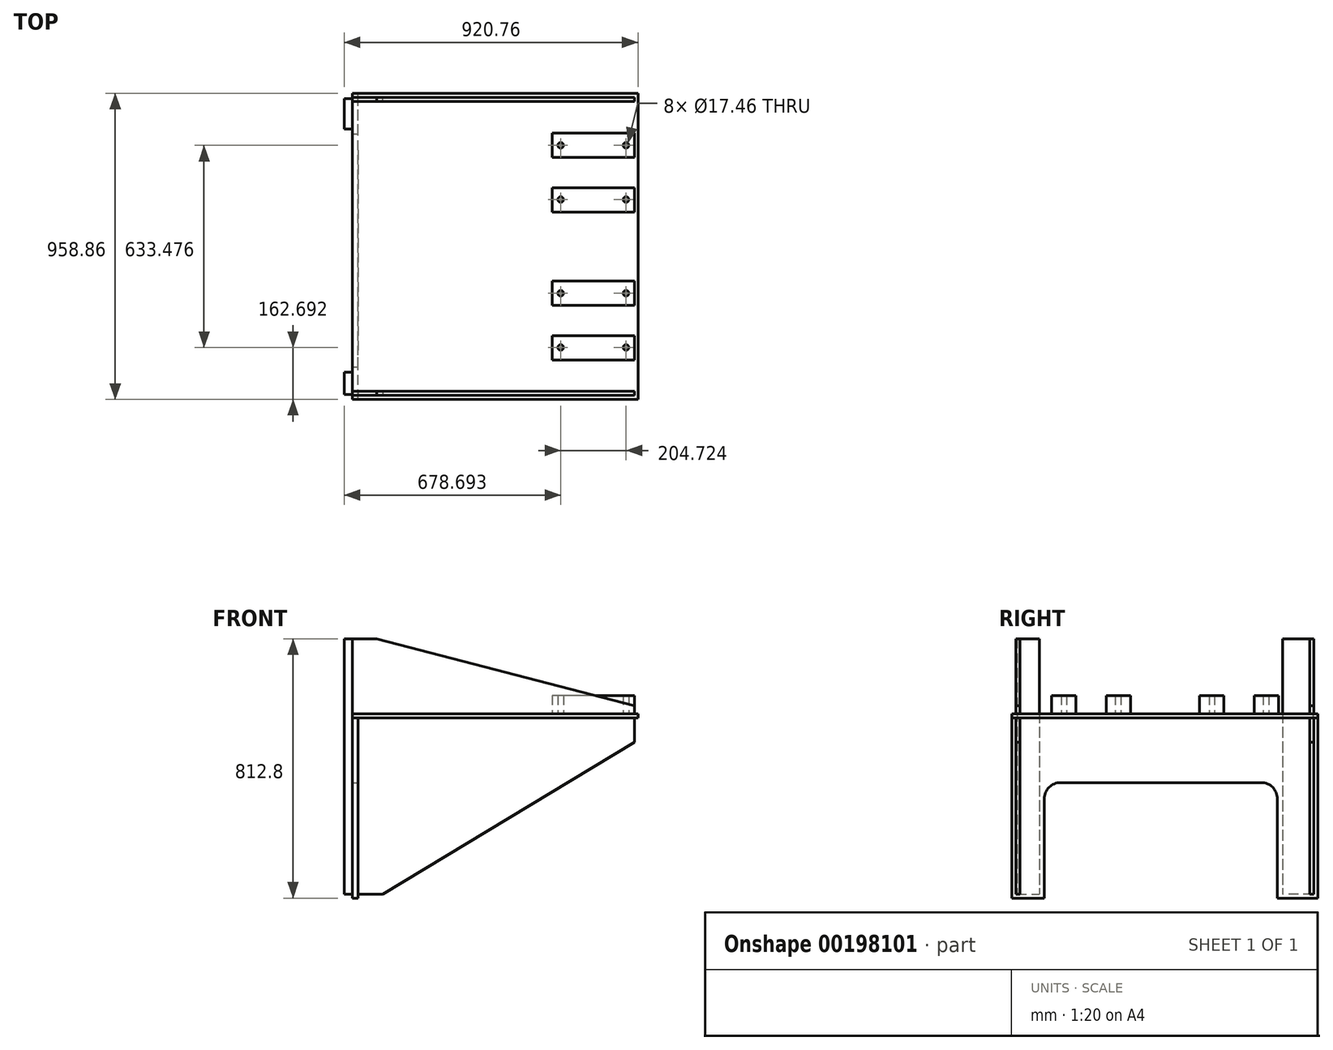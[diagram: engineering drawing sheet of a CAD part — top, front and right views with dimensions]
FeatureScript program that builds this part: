
annotation { "Feature Type Name" : "Feature", "Feature Type Description" : "" }
export const myFeature = defineFeature(function(context is Context, id is Id, definition is map)
    precondition{}
    {
        {
            var Q0;
            Q0=qCreatedBy(makeId("Top.planeOp"),FACE);
            var sketch = newSketch(context, id + "F0", { "sketchPlane" : qUnion([Q0])});
            skLineSegment(sketch, "E0.bottom", {"start": v(-447.67, 479.43) * mm, "end": v(447.68, 479.43) * mm});
            skLineSegment(sketch, "E0.top", {"start": v(-447.68, -479.43) * mm, "end": v(447.68, -479.43) * mm});
            skLineSegment(sketch, "E0.left", {"start": v(-447.67, 479.43) * mm, "end": v(-447.68, -479.43) * mm});
            skLineSegment(sketch, "E0.right", {"start": v(447.68, 479.42) * mm, "end": v(447.68, -479.43) * mm});
            skPoint(sketch, "E0.middle", {"position": v(0, 0) * mm});
            skSolve(sketch);
        }
        {
            var Q0;
            Q0 = qSketchRegion(id + "F0", true);
            extrude(context, id + "F1", {"entities" : qUnion([Q0]), "depth" : 12.7 * mm});
        }
        {
            var Q0;
            Q0=makeQuery(id+"F1.opExtrude","CAP_FACE",FACE,{"disambiguationData":[OSD([sQuery(id+"F0.wireOp",EDGE,"E0.bottom"),sQuery(id+"F0.wireOp",EDGE,"E0.top"),sQuery(id+"F0.wireOp",EDGE,"E0.left"),sQuery(id+"F0.wireOp",EDGE,"E0.right")])],"isStart":false});
            var sketch = newSketch(context, id + "F2", { "sketchPlane" : qUnion([Q0])});
            skLineSegment(sketch, "E1", {"start": v(-705.76, 0) * mm, "end": v(723.96, 0) * mm, "construction": true});
            skLineSegment(sketch, "E2.0", {"start": v(-447.68, -479.43) * mm, "end": v(447.68, -479.43) * mm, "construction": true});
            skLineSegment(sketch, "E3.0", {"start": v(-447.68, -466.73) * mm, "end": v(447.68, -466.73) * mm, "construction": true});
            skLineSegment(sketch, "E4.0", {"start": v(447.68, 479.42) * mm, "end": v(447.68, -479.43) * mm, "construction": true});
            skLineSegment(sketch, "E5.0", {"start": v(436.5, 479.42) * mm, "end": v(436.5, -479.43) * mm, "construction": true});
            skLineSegment(sketch, "E6.0", {"start": v(-447.67, 479.43) * mm, "end": v(-447.68, -479.43) * mm, "construction": true});
            skLineSegment(sketch, "E7.bottom", {"start": v(436.5, -466.73) * mm, "end": v(-447.68, -466.73) * mm});
            skLineSegment(sketch, "E7.top", {"start": v(436.5, -454.03) * mm, "end": v(-447.68, -454.03) * mm});
            skLineSegment(sketch, "E7.left", {"start": v(436.5, -466.73) * mm, "end": v(436.5, -454.03) * mm});
            skLineSegment(sketch, "E7.right", {"start": v(-447.68, -466.73) * mm, "end": v(-447.68, -454.03) * mm});
            skSolve(sketch);
        }
        {
            var Q0;
            Q0 = qSketchRegion(id + "F2", true);
            extrude(context, id + "F3", {"entities" : qUnion([Q0]), "depth" : 234.95 * mm});
        }
        {
            var Q0;
            Q0=makeQuery(id+"F3.opExtrude","SWEPT_FACE",FACE,{"disambiguationData":[OSD([sQuery(id+"F2.wireOp",EDGE,"E7.bottom")])]});
            var sketch = newSketch(context, id + "F4", { "sketchPlane" : qUnion([Q0])});
            skLineSegment(sketch, "E8.0", {"start": v(-447.68, 247.65) * mm, "end": v(-447.68, 12.7) * mm, "construction": true});
            skLineSegment(sketch, "E9.0", {"start": v(-447.68, 12.7) * mm, "end": v(447.68, 12.7) * mm, "construction": true});
            skLineSegment(sketch, "E10.0", {"start": v(-371.48, 247.65) * mm, "end": v(-371.48, 12.7) * mm, "construction": true});
            skLineSegment(sketch, "E11.0", {"start": v(-447.68, 38.1) * mm, "end": v(447.68, 38.1) * mm, "construction": true});
            skLineSegment(sketch, "E12", {"start": v(-371.48, 247.65) * mm, "end": v(436.5, 38.1) * mm});
            skLineSegment(sketch, "E13", {"start": v(436.5, 38.1) * mm, "end": v(436.5, 247.65) * mm});
            skLineSegment(sketch, "E14", {"start": v(436.5, 247.65) * mm, "end": v(-371.48, 247.65) * mm});
            skSolve(sketch);
        }
        {
            var Q0;
            Q0 = qSketchRegion(id + "F4", true);
            extrude(context, id + "F5", {"entities" : qUnion([Q0]), "operationType" : NewBodyOperationType.REMOVE, "endBound" : BoundingType.THROUGH_ALL, "oppositeDirection" : true, "depth" : 25.4 * mm});
        }
        {
            var Q0;
            Q0=makeQuery(id+"F3.opExtrude","SWEPT_BODY",BODY,{"disambiguationData":[OSD([sQuery(id+"F2.wireOp",EDGE,"E7.bottom"),sQuery(id+"F2.wireOp",EDGE,"E7.top"),sQuery(id+"F2.wireOp",EDGE,"E7.left"),sQuery(id+"F2.wireOp",EDGE,"E7.right")])]});
            var Q1;
            Q1=qCreatedBy(makeId("Front.planeOp"),FACE);
            mirror(context, id + "F6", {"entities" : qUnion([Q0]), "mirrorPlane" : qUnion([Q1])});
        }
        {
            var Q0;
            Q0=makeQuery(id+"F3.opExtrude","SWEPT_FACE",FACE,{"disambiguationData":[OSD([sQuery(id+"F2.wireOp",EDGE,"E7.bottom")])]});
            var sketch = newSketch(context, id + "F7", { "sketchPlane" : qUnion([Q0])});
            skLineSegment(sketch, "E15.0", {"start": v(436.5, 38.1) * mm, "end": v(436.5, -76.2) * mm, "construction": true});
            skLineSegment(sketch, "E16", {"start": v(-447.68, 22.62) * mm, "end": v(-447.68, -552.45) * mm, "construction": true});
            skLineSegment(sketch, "E17.0", {"start": v(-447.68, 0) * mm, "end": v(447.68, 0) * mm, "construction": true});
            skLineSegment(sketch, "E18.0", {"start": v(-447.68, -552.45) * mm, "end": v(447.68, -552.45) * mm, "construction": true});
            skPoint(sketch, "E19.orphan", {"position": v(436.5, 12.7) * mm});
            skLineSegment(sketch, "E20.0", {"start": v(-428.63, 22.62) * mm, "end": v(-428.63, -552.45) * mm, "construction": true});
            skLineSegment(sketch, "E21.bottom", {"start": v(-428.63, -552.45) * mm, "end": v(436.5, -552.45) * mm});
            skLineSegment(sketch, "E21.top", {"start": v(-428.63, 0) * mm, "end": v(436.5, 0) * mm});
            skLineSegment(sketch, "E21.left", {"start": v(-428.63, -552.45) * mm, "end": v(-428.63, 0) * mm});
            skLineSegment(sketch, "E21.right", {"start": v(436.5, -76.2) * mm, "end": v(436.5, 0) * mm});
            skLineSegment(sketch, "E22.0", {"start": v(-447.68, -76.2) * mm, "end": v(447.68, -76.2) * mm, "construction": true});
            skLineSegment(sketch, "E23.0", {"start": v(-352.43, 22.62) * mm, "end": v(-352.43, -552.45) * mm, "construction": true});
            skLineSegment(sketch, "E24", {"start": v(-352.43, -552.45) * mm, "end": v(436.5, -76.2) * mm});
            skSolve(sketch);
        }
        {
            var Q0;
            Q0 = qSketchRegion(id + "F7", true);
            extrude(context, id + "F8", {"entities" : qUnion([Q0]), "oppositeDirection" : true, "depth" : 12.7 * mm});
        }
        {
            var Q0;
            Q0=makeQuery(id+"F8.opExtrude","SWEPT_BODY",BODY,{"disambiguationData":[OSD([sQuery(id+"F7.wireOp",EDGE,"E21.bottom"),sQuery(id+"F7.wireOp",EDGE,"E21.top"),sQuery(id+"F7.wireOp",EDGE,"E21.left"),sQuery(id+"F7.wireOp",EDGE,"E21.right"),sQuery(id+"F7.wireOp",EDGE,"E24")])]});
            var Q1;
            Q1=qCreatedBy(makeId("Front.planeOp"),FACE);
            mirror(context, id + "F9", {"entities" : qUnion([Q0]), "mirrorPlane" : qUnion([Q1])});
        }
        {
            var Q0;
            Q0=makeQuery(id+"F8.opExtrude","SWEPT_FACE",FACE,{"disambiguationData":[OSD([sQuery(id+"F7.wireOp",EDGE,"E21.left")])]});
            var sketch = newSketch(context, id + "F10", { "sketchPlane" : qUnion([Q0])});
            skLineSegment(sketch, "E25.0", {"start": v(-479.43, 0) * mm, "end": v(479.43, 0) * mm, "construction": true});
            skLineSegment(sketch, "E26.bottom", {"start": v(479.43, 0) * mm, "end": v(-479.43, 0) * mm});
            skLineSegment(sketch, "E26.top", {"start": v(479.43, -565.15) * mm, "end": v(377.83, -565.15) * mm});
            skLineSegment(sketch, "E26.left", {"start": v(479.43, 0) * mm, "end": v(479.43, -565.15) * mm});
            skLineSegment(sketch, "E26.right", {"start": v(-479.43, 0) * mm, "end": v(-479.43, -565.15) * mm});
            skLineSegment(sketch, "E27", {"start": v(0, 122.56) * mm, "end": v(0, -666.88) * mm, "construction": true});
            skLineSegment(sketch, "E28.top", {"start": v(-301.62, -203.2) * mm, "end": v(327.03, -203.2) * mm});
            skLineSegment(sketch, "E28.left", {"start": v(-352.42, -565.15) * mm, "end": v(-352.42, -254) * mm});
            skLineSegment(sketch, "E28.right", {"start": v(377.83, -565.15) * mm, "end": v(377.83, -254) * mm});
            skLineSegment(sketch, "E29.trimOffspring", {"start": v(-352.42, -565.15) * mm, "end": v(-479.42, -565.15) * mm});
            skPoint(sketch, "E30.visualSharp", {"position": v(-352.42, -203.2) * mm});
            skArc(sketch, "E30.filletArc", {"start": v(-301.62, -203.2) * mm, "mid": v(-337.55, -218.08) * mm, "end": v(-352.42, -254) * mm});
            skPoint(sketch, "E31.visualSharp", {"position": v(377.83, -203.2) * mm});
            skArc(sketch, "E31.filletArc", {"start": v(377.83, -254) * mm, "mid": v(362.95, -218.08) * mm, "end": v(327.03, -203.2) * mm});
            skSolve(sketch);
        }
        {
            var Q0;
            Q0 = qSketchRegion(id + "F10", true);
            extrude(context, id + "F11", {"entities" : qUnion([Q0]), "depth" : 19.05 * mm});
        }
        {
            var Q0;
            Q0=makeQuery(id+"F11.opExtrude","CAP_FACE",FACE,{"disambiguationData":[OSD([sQuery(id+"F10.wireOp",EDGE,"E26.bottom"),sQuery(id+"F10.wireOp",EDGE,"E26.top"),sQuery(id+"F10.wireOp",EDGE,"E26.left"),sQuery(id+"F10.wireOp",EDGE,"E26.right"),sQuery(id+"F10.wireOp",EDGE,"E28.top"),sQuery(id+"F10.wireOp",EDGE,"E28.left"),sQuery(id+"F10.wireOp",EDGE,"E28.right"),sQuery(id+"F10.wireOp",EDGE,"E29.trimOffspring"),sQuery(id+"F10.wireOp",EDGE,"E30.filletArc"),sQuery(id+"F10.wireOp",EDGE,"E31.filletArc")])],"isStart":false});
            var sketch = newSketch(context, id + "F12", { "sketchPlane" : qUnion([Q0])});
            skLineSegment(sketch, "E32.0", {"start": v(-454.03, 247.65) * mm, "end": v(-466.73, 247.65) * mm, "construction": true});
            skPoint(sketch, "E33.0", {"position": v(-466.73, 130.17) * mm});
            skLineSegment(sketch, "E34.0", {"start": v(-466.73, 247.65) * mm, "end": v(-466.73, 12.7) * mm, "construction": true});
            skLineSegment(sketch, "E35.bottom", {"start": v(-463.55, 247.65) * mm, "end": v(-368.3, 247.65) * mm});
            skLineSegment(sketch, "E35.top", {"start": v(-463.55, -552.45) * mm, "end": v(-368.3, -552.45) * mm});
            skLineSegment(sketch, "E35.left", {"start": v(-463.55, 247.65) * mm, "end": v(-463.55, -552.45) * mm});
            skLineSegment(sketch, "E35.right", {"start": v(-368.3, 247.65) * mm, "end": v(-368.3, -552.45) * mm});
            skLineSegment(sketch, "E36", {"start": v(0, 415.78) * mm, "end": v(0, -629.1) * mm, "construction": true});
            skLineSegment(sketch, "E37.MirrorCS", {"start": v(454.03, 247.65) * mm, "end": v(466.73, 247.65) * mm, "construction": true});
            skPoint(sketch, "E38.MirrorP", {"position": v(466.73, 130.17) * mm});
            skLineSegment(sketch, "E39.MirrorCS", {"start": v(466.73, 247.65) * mm, "end": v(466.73, 12.7) * mm, "construction": true});
            skLineSegment(sketch, "E40.MirrorCS", {"start": v(463.55, 247.65) * mm, "end": v(393.7, 247.65) * mm});
            skLineSegment(sketch, "E41.MirrorCS", {"start": v(463.55, -552.45) * mm, "end": v(393.7, -552.45) * mm});
            skLineSegment(sketch, "E42.MirrorCS", {"start": v(463.55, 247.65) * mm, "end": v(463.55, -552.45) * mm});
            skLineSegment(sketch, "E43", {"start": v(393.7, 247.65) * mm, "end": v(393.7, -552.45) * mm});
            skPoint(sketch, "E44.orphan", {"position": v(368.3, -552.45) * mm});
            skSolve(sketch);
        }
        {
            var Q0;
            Q0 = qSketchRegion(id + "F12", true);
            extrude(context, id + "F13", {"entities" : qUnion([Q0]), "depth" : 25.4 * mm});
        }
        {
            var Q0;
            Q0=makeQuery(id+"F1.opExtrude","CAP_FACE",FACE,{"disambiguationData":[OSD([sQuery(id+"F0.wireOp",EDGE,"E0.bottom"),sQuery(id+"F0.wireOp",EDGE,"E0.top"),sQuery(id+"F0.wireOp",EDGE,"E0.left"),sQuery(id+"F0.wireOp",EDGE,"E0.right")])],"isStart":false});
            var sketch = newSketch(context, id + "F14", { "sketchPlane" : qUnion([Q0])});
            skLineSegment(sketch, "E45", {"start": v(528.24, 0) * mm, "end": v(-607.88, 0) * mm, "construction": true});
            skLineSegment(sketch, "E46.0", {"start": v(447.68, 479.42) * mm, "end": v(447.68, -479.43) * mm, "construction": true});
            skLineSegment(sketch, "E47.0", {"start": v(436.5, 479.42) * mm, "end": v(436.5, -479.43) * mm, "construction": true});
            skLineSegment(sketch, "E48.0", {"start": v(528.24, -107.95) * mm, "end": v(-607.88, -107.95) * mm, "construction": true});
            skLineSegment(sketch, "E49.0", {"start": v(528.24, -184.15) * mm, "end": v(-607.88, -184.15) * mm, "construction": true});
            skLineSegment(sketch, "E50.0", {"start": v(528.24, -279.4) * mm, "end": v(-607.88, -279.4) * mm, "construction": true});
            skLineSegment(sketch, "E51.0", {"start": v(441.33, 473.07) * mm, "end": v(-441.32, 473.07) * mm, "construction": true});
            skLineSegment(sketch, "E51.1", {"start": v(441.33, -473.08) * mm, "end": v(441.33, 473.07) * mm, "construction": true});
            skLineSegment(sketch, "E51.2", {"start": v(-441.33, -473.08) * mm, "end": v(441.33, -473.08) * mm, "construction": true});
            skLineSegment(sketch, "E51.3", {"start": v(-441.32, 473.08) * mm, "end": v(-441.33, -473.08) * mm, "construction": true});
            skLineSegment(sketch, "E52.0", {"start": v(528.24, -355.6) * mm, "end": v(-607.88, -355.6) * mm, "construction": true});
            skLineSegment(sketch, "E53.bottom", {"start": v(436.5, -107.95) * mm, "end": v(179.45, -107.95) * mm});
            skLineSegment(sketch, "E53.top", {"start": v(436.5, -184.15) * mm, "end": v(179.45, -184.15) * mm});
            skLineSegment(sketch, "E53.left", {"start": v(436.5, -107.95) * mm, "end": v(436.5, -184.15) * mm});
            skLineSegment(sketch, "E53.right", {"start": v(179.45, -107.95) * mm, "end": v(179.45, -184.15) * mm});
            skLineSegment(sketch, "E54.bottom", {"start": v(436.5, -279.4) * mm, "end": v(179.45, -279.4) * mm});
            skLineSegment(sketch, "E54.top", {"start": v(436.5, -355.6) * mm, "end": v(179.45, -355.6) * mm});
            skLineSegment(sketch, "E54.left", {"start": v(436.5, -279.4) * mm, "end": v(436.5, -355.6) * mm});
            skLineSegment(sketch, "E54.right", {"start": v(179.45, -279.4) * mm, "end": v(179.45, -355.6) * mm});
            skLineSegment(sketch, "E55", {"start": v(307.98, -184.15) * mm, "end": v(307.97, -279.4) * mm, "construction": true});
            skLineSegment(sketch, "E56", {"start": v(307.98, -231.78) * mm, "end": v(148.46, -231.78) * mm, "construction": true});
            skLineSegment(sketch, "E57.0", {"start": v(307.97, -146.81) * mm, "end": v(148.46, -146.81) * mm, "construction": true});
            skLineSegment(sketch, "E58.0", {"start": v(205.61, -146.81) * mm, "end": v(205.61, -279.4) * mm, "construction": true});
            skCircle(sketch, "E59", {"center": v(205.61, -146.81) * mm, "radius": 8.73 * mm});
            skCircle(sketch, "E60.MirrorC", {"center": v(410.34, -146.81) * mm, "radius": 8.73 * mm});
            skCircle(sketch, "E61.MirrorC", {"center": v(205.61, -316.74) * mm, "radius": 8.73 * mm});
            skCircle(sketch, "E62.MirrorC", {"center": v(410.34, -316.74) * mm, "radius": 8.73 * mm});
            skCircle(sketch, "E63.MirrorC", {"center": v(205.61, 146.81) * mm, "radius": 8.73 * mm});
            skCircle(sketch, "E64.MirrorC", {"center": v(205.61, 316.74) * mm, "radius": 8.73 * mm});
            skCircle(sketch, "E65.MirrorC", {"center": v(410.34, 316.74) * mm, "radius": 8.73 * mm});
            skCircle(sketch, "E66.MirrorC", {"center": v(410.34, 146.81) * mm, "radius": 8.73 * mm});
            skLineSegment(sketch, "E67.MirrorCS", {"start": v(205.61, 146.81) * mm, "end": v(205.61, 279.4) * mm, "construction": true});
            skLineSegment(sketch, "E68.MirrorCS", {"start": v(436.5, 107.95) * mm, "end": v(179.45, 107.95) * mm});
            skLineSegment(sketch, "E69.MirrorCS", {"start": v(436.5, 184.15) * mm, "end": v(179.45, 184.15) * mm});
            skLineSegment(sketch, "E70.MirrorCS", {"start": v(307.98, 146.81) * mm, "end": v(148.46, 146.81) * mm, "construction": true});
            skLineSegment(sketch, "E71.MirrorCS", {"start": v(307.98, 184.15) * mm, "end": v(307.98, 279.4) * mm, "construction": true});
            skLineSegment(sketch, "E72.MirrorCS", {"start": v(436.5, 279.4) * mm, "end": v(436.5, 355.6) * mm});
            skLineSegment(sketch, "E73.MirrorCS", {"start": v(179.45, 279.4) * mm, "end": v(179.45, 355.6) * mm});
            skLineSegment(sketch, "E74.MirrorCS", {"start": v(436.5, 355.6) * mm, "end": v(179.45, 355.6) * mm});
            skLineSegment(sketch, "E75.MirrorCS", {"start": v(436.5, 107.95) * mm, "end": v(436.5, 184.15) * mm});
            skLineSegment(sketch, "E76.MirrorCS", {"start": v(179.45, 107.95) * mm, "end": v(179.45, 184.15) * mm});
            skLineSegment(sketch, "E77.MirrorCS", {"start": v(307.98, 231.78) * mm, "end": v(148.46, 231.78) * mm, "construction": true});
            skLineSegment(sketch, "E78.MirrorCS", {"start": v(436.5, 279.4) * mm, "end": v(179.45, 279.4) * mm});
            skSolve(sketch);
        }
        {
            var Q0;
            Q0 = qSketchRegion(id + "F14", true);
            extrude(context, id + "F15", {"entities" : qUnion([Q0]), "depth" : 57.15 * mm});
        }
    });
